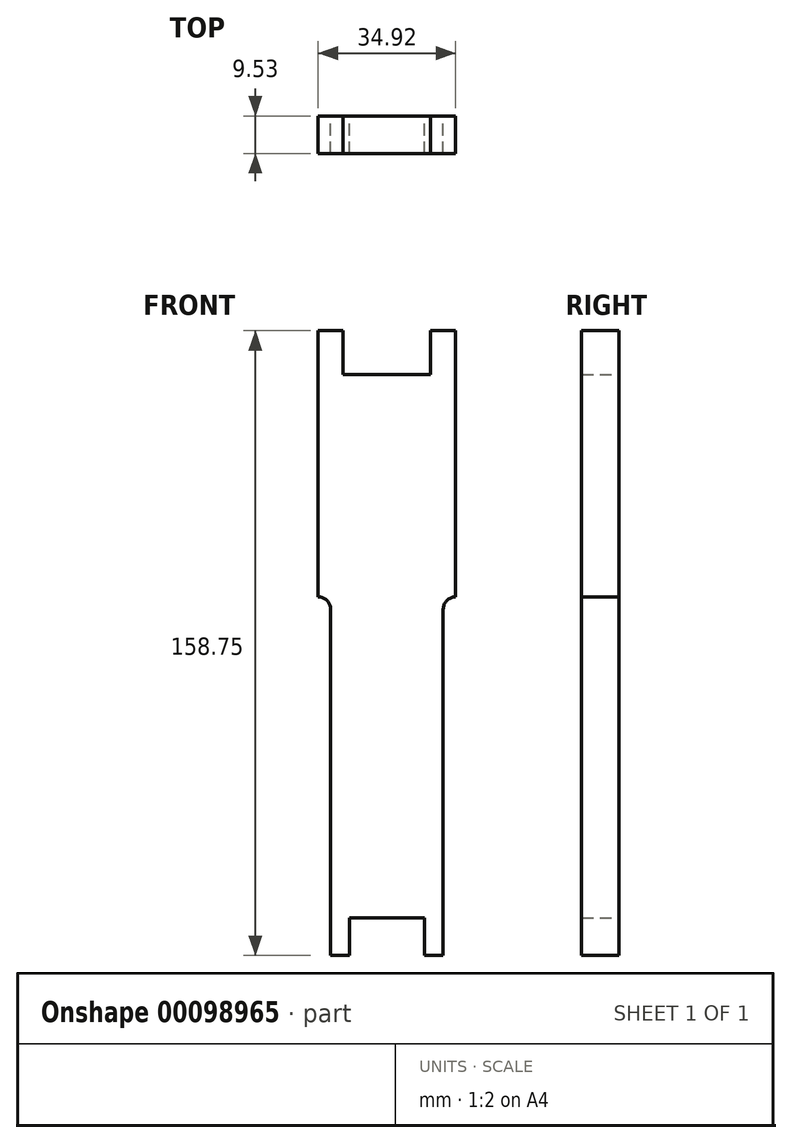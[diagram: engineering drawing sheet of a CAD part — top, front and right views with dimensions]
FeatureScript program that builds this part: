
annotation { "Feature Type Name" : "Feature", "Feature Type Description" : "" }
export const myFeature = defineFeature(function(context is Context, id is Id, definition is map)
    precondition{}
    {
        {
            var Q0;
            Q0=qCreatedBy(makeId("Front.planeOp"),FACE);
            var sketch = newSketch(context, id + "F0", { "sketchPlane" : qUnion([Q0])});
            skLineSegment(sketch, "E0", {"start": v(0, 0) * mm, "end": v(9.53, 0) * mm});
            skLineSegment(sketch, "E1", {"start": v(9.53, 0) * mm, "end": v(9.53, -9.52) * mm});
            skLineSegment(sketch, "E2", {"start": v(9.53, -9.52) * mm, "end": v(14.29, -9.52) * mm});
            skLineSegment(sketch, "E3", {"start": v(14.29, -9.52) * mm, "end": v(14.29, 78.43) * mm});
            skLineSegment(sketch, "E4", {"start": v(17.46, 81.6) * mm, "end": v(17.46, 81.6) * mm});
            skLineSegment(sketch, "E5", {"start": v(17.46, 81.6) * mm, "end": v(17.46, 149.22) * mm});
            skLineSegment(sketch, "E6", {"start": v(17.46, 149.22) * mm, "end": v(11.11, 149.22) * mm});
            skLineSegment(sketch, "E7", {"start": v(11.11, 149.22) * mm, "end": v(11.11, 138.11) * mm});
            skLineSegment(sketch, "E8", {"start": v(11.11, 138.11) * mm, "end": v(0, 138.11) * mm});
            skLineSegment(sketch, "E9", {"start": v(0, 138.11) * mm, "end": v(0, 0) * mm, "construction": true});
            skLineSegment(sketch, "E10.MirrorCS", {"start": v(-11.11, 138.11) * mm, "end": v(0, 138.11) * mm});
            skLineSegment(sketch, "E11.MirrorCS", {"start": v(-11.11, 149.22) * mm, "end": v(-11.11, 138.11) * mm});
            skLineSegment(sketch, "E12.MirrorCS", {"start": v(-17.46, 149.22) * mm, "end": v(-11.11, 149.22) * mm});
            skLineSegment(sketch, "E13.MirrorCS", {"start": v(-17.46, 81.6) * mm, "end": v(-17.46, 149.22) * mm});
            skLineSegment(sketch, "E14.MirrorCS", {"start": v(-17.46, 81.6) * mm, "end": v(-17.46, 81.6) * mm});
            skLineSegment(sketch, "E15.MirrorCS", {"start": v(-14.29, -9.52) * mm, "end": v(-14.29, 78.43) * mm});
            skLineSegment(sketch, "E16.MirrorCS", {"start": v(-9.53, -9.52) * mm, "end": v(-14.29, -9.53) * mm});
            skLineSegment(sketch, "E17.MirrorCS", {"start": v(-9.53, 0) * mm, "end": v(-9.53, -9.52) * mm});
            skLineSegment(sketch, "E18.MirrorCS", {"start": v(0, 0) * mm, "end": v(-9.53, 0) * mm});
            skPoint(sketch, "E19.visualSharp", {"position": v(14.29, 81.6) * mm});
            skArc(sketch, "E19.filletArc", {"start": v(17.46, 81.6) * mm, "mid": v(15.22, 80.67) * mm, "end": v(14.29, 78.43) * mm});
            skPoint(sketch, "E20.visualSharp", {"position": v(-14.29, 81.6) * mm});
            skArc(sketch, "E20.filletArc", {"start": v(-14.29, 78.43) * mm, "mid": v(-15.22, 80.67) * mm, "end": v(-17.46, 81.6) * mm});
            skSolve(sketch);
        }
        {
            var Q0;
            Q0=makeQuery(id+"F0.imprint","IMPRINT",FACE,{"disambiguationData":[TD([[makeQuery(id+"F0.imprint","IMPRINT",EDGE,{"derivedFrom":sQuery(id+"F0.wireOp",EDGE,"E0")}),1.0]])]});
            extrude(context, id + "F1", {"entities" : qUnion([Q0]), "depth" : 9.52 * mm});
        }
    });
